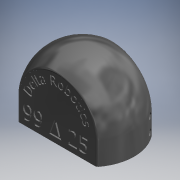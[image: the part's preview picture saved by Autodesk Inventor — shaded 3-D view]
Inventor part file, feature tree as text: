
AUTODESK INVENTOR PART (.ipt)
format: ipt  version: 2019 (Build 230136000, 136)  size: 745,472 bytes
history: native  units: mm (DEFAULTED — no unit token found)
features: sketch x11, extrude x10, plane x5, mirror x3, revolve x1, fillet x1
ambient origin geometry x8: Origin, YZ Plane, XZ Plane, XY Plane, X Axis, Y Axis, Z Axis, Center Point
bodies: Solid1 (feature_tree)
feature tree (31):
  extrude  "Extrusion1"  Depth=88.9mm
  extrude  "Extrusion2"  Depth=25.4mm
  extrude  "Extrusion3"  Depth=3.175mm TaperAngle=0.0deg
  plane  "Work Plane1"
  mirror  "Mirror1"
  plane  "Work Plane2"
  revolve  "Revolution1"  [1 undecoded]
  extrude  "Extrusion4"  Depth=44.45mm
  plane  "Work Plane3"
  mirror  "Mirror2"
  fillet  "Fillet1"  Radius=44.45mm
  sketch  "Sketch7"  dims[d14=180.0deg d15=25.4mm d16=0.0mm]
  extrude  "Extrusion5"  Depth=25.4mm TaperAngle=0.0deg
  extrude  "Extrusion6"  Depth=3.175mm
  plane  "Work Plane4"
  extrude  "Extrusion7"  Depth=8.001mm
  plane  "Work Plane5"
  mirror  "Mirror3"
  extrude  "Extrusion8"  Depth=6.35mm
  extrude  "Extrusion9"  Depth=3.048mm
  extrude  "Extrusion10"  Depth=3.175mm TaperAngle=0.0deg
  sketch  "Sketch1"  dims[d0=82.55mm d1=88.9mm]
  sketch  "Sketch2"  dims[d2=25.4mm d3=25.4mm]
  sketch  "Sketch3"  dims[d4=59.69mm d5=0.0mm d6=3.175mm d7=0.0mm]
  sketch  "Sketch5"  dims[d8=12.7mm d9=25.4mm]
  sketch  "Sketch6"  dims[d10=9.525mm d11=0.0mm d12=44.45mm d13=44.45mm]
  sketch  "Sketch8"  dims[d17=3.175mm d18=6.35mm]
  sketch  "Sketch9"  dims[d19=6.35mm d20=8.001mm]
  sketch  "Sketch10"  dims[d21=24.003mm d22=6.35mm]
  sketch  "Sketch11"  dims[d23=2.54mm d24=0.0mm d25=3.048mm]
  sketch  "Sketch12"  dims[d26=3.048mm d27=2.54mm d28=0.0mm d29=6.35mm d30=6.35mm d31=19.05mm d32=0.0mm d33=38.1mm d34=1.27mm d35=0.0mm d36=1.5875mm d37=0.0mm d38=3.175mm d39=3.175mm d40=3.175mm d41=19.05mm d42=12.7mm d43=12.7mm d44=12.7mm d45=85.725mm d46=0.0mm d47=25.4mm d48=0.0mm]
note: 1 required parameter value undecoded (feature->parameter linkage not recoverable at this tier; creation-order binding heuristic only, values carry confidence <= 0.55)
